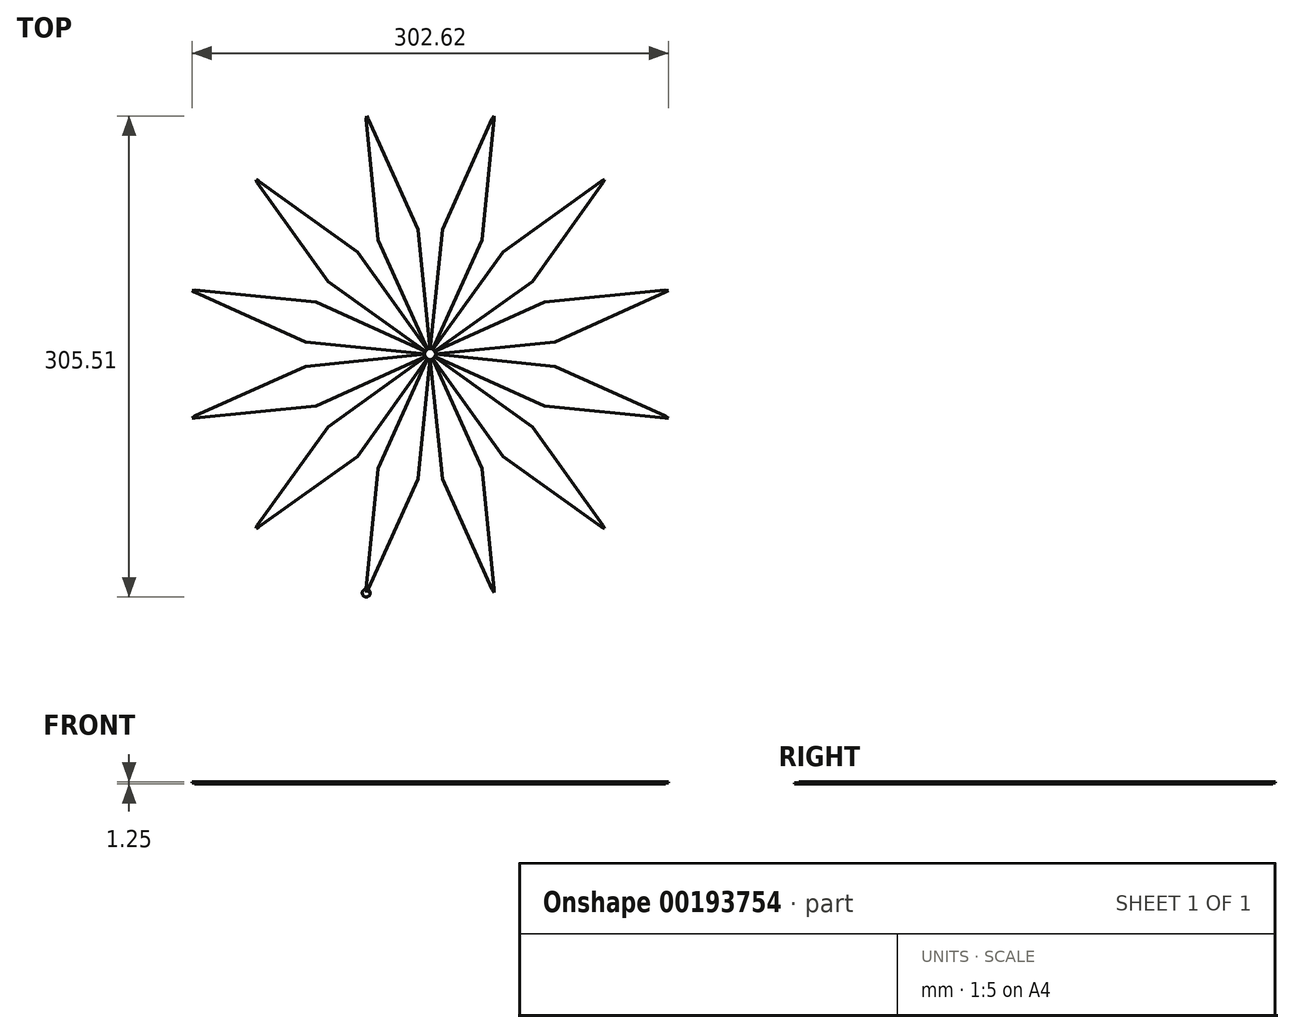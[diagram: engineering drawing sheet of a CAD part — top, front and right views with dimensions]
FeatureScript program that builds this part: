
annotation { "Feature Type Name" : "Feature", "Feature Type Description" : "" }
export const myFeature = defineFeature(function(context is Context, id is Id, definition is map)
    precondition{}
    {
        {
            var Q0;
            Q0=qCreatedBy(makeId("Top.planeOp"),FACE);
            var sketch = newSketch(context, id + "F2", { "sketchPlane" : qUnion([Q0])});
            skCircle(sketch, "E0", {"center": v(0, 0) * mm, "radius": 2.59 * mm});
            skLineSegment(sketch, "E1", {"start": v(0, 0) * mm, "end": v(-1.3, -2.24) * mm});
            skLineSegment(sketch, "E2", {"start": v(0, 0) * mm, "end": v(0, -2.59) * mm});
            skLineSegment(sketch, "E3", {"start": v(2.24, -1.3) * mm, "end": v(2.24, -1.3) * mm});
            skLineSegment(sketch, "E4", {"start": v(1.3, -2.24) * mm, "end": v(1.3, -2.24) * mm});
            skLineSegment(sketch, "E5", {"start": v(0, -2.59) * mm, "end": v(-1.3, -2.24) * mm});
            skLineSegment(sketch, "E6", {"start": v(0, 0) * mm, "end": v(-2.59, 0) * mm});
            skLineSegment(sketch, "E7", {"start": v(0, 0) * mm, "end": v(-2.24, -1.3) * mm});
            skLineSegment(sketch, "E8", {"start": v(-2.59, 0) * mm, "end": v(-2.24, -1.3) * mm});
            skLineSegment(sketch, "E9", {"start": v(-2.24, -1.3) * mm, "end": v(-1.3, -2.24) * mm});
            skLineSegment(sketch, "E10", {"start": v(-1.3, -2.24) * mm, "end": v(-40.67, -149.2) * mm, "construction": true});
            skLineSegment(sketch, "E11", {"start": v(0, -2.59) * mm, "end": v(-39.38, -149.55) * mm, "construction": true});
            skPoint(sketch, "E12", {"position": v(-19.69, -76.07) * mm});
            skPoint(sketch, "E13", {"position": v(-20.98, -75.72) * mm});
            skLineSegment(sketch, "E14", {"start": v(-7.69, -79.28) * mm, "end": v(-32.98, -72.5) * mm, "construction": true});
            skLineSegment(sketch, "E15", {"start": v(-19.69, -76.07) * mm, "end": v(-20.98, -75.72) * mm, "construction": true});
            skPoint(sketch, "E16", {"position": v(-20.34, -75.9) * mm});
            skLineSegment(sketch, "E17", {"start": v(-32.98, -72.5) * mm, "end": v(-40.67, -149.2) * mm});
            skLineSegment(sketch, "E18", {"start": v(-40.67, -149.2) * mm, "end": v(-39.38, -149.55) * mm, "construction": true});
            skLineSegment(sketch, "E19", {"start": v(-39.38, -149.55) * mm, "end": v(-7.69, -79.28) * mm});
            skLineSegment(sketch, "E20", {"start": v(-7.69, -79.28) * mm, "end": v(0, -2.59) * mm});
            skLineSegment(sketch, "E21", {"start": v(-32.98, -72.5) * mm, "end": v(-1.3, -2.24) * mm});
            skLineSegment(sketch, "E22.MirrorCS", {"start": v(-64.82, -46.3) * mm, "end": v(-2.24, -1.3) * mm});
            skLineSegment(sketch, "E23.MirrorCS", {"start": v(-46.3, -64.82) * mm, "end": v(-1.3, -2.24) * mm});
            skLineSegment(sketch, "E24.MirrorCS", {"start": v(-109.82, -108.88) * mm, "end": v(-64.82, -46.3) * mm});
            skLineSegment(sketch, "E25.MirrorCS", {"start": v(-46.3, -64.82) * mm, "end": v(-108.88, -109.82) * mm});
            skLineSegment(sketch, "E26.MirrorCS", {"start": v(-108.88, -109.82) * mm, "end": v(-109.82, -108.88) * mm, "construction": true});
            skLineSegment(sketch, "E27.MirrorCS", {"start": v(-72.5, -32.98) * mm, "end": v(-2.24, -1.3) * mm});
            skLineSegment(sketch, "E28.MirrorCS", {"start": v(-79.28, -7.69) * mm, "end": v(-2.59, 0) * mm});
            skLineSegment(sketch, "E29.MirrorCS", {"start": v(-79.28, -7.69) * mm, "end": v(-149.55, -39.38) * mm});
            skLineSegment(sketch, "E30.MirrorCS", {"start": v(-149.2, -40.67) * mm, "end": v(-72.5, -32.98) * mm});
            skLineSegment(sketch, "E31.MirrorCS", {"start": v(-149.55, -39.38) * mm, "end": v(-149.2, -40.67) * mm, "construction": true});
            skLineSegment(sketch, "E32.MirrorCS", {"start": v(7.69, -79.28) * mm, "end": v(0, -2.59) * mm});
            skLineSegment(sketch, "E33.MirrorCS", {"start": v(39.38, -149.55) * mm, "end": v(7.69, -79.28) * mm});
            skLineSegment(sketch, "E34.MirrorCS", {"start": v(32.98, -72.5) * mm, "end": v(40.67, -149.2) * mm});
            skLineSegment(sketch, "E35.MirrorCS", {"start": v(32.98, -72.5) * mm, "end": v(1.3, -2.24) * mm});
            skLineSegment(sketch, "E36.MirrorCS", {"start": v(40.67, -149.2) * mm, "end": v(39.38, -149.55) * mm, "construction": true});
            skLineSegment(sketch, "E37.MirrorCS", {"start": v(46.3, -64.82) * mm, "end": v(1.3, -2.24) * mm});
            skLineSegment(sketch, "E38.MirrorCS", {"start": v(109.82, -108.88) * mm, "end": v(64.82, -46.3) * mm});
            skLineSegment(sketch, "E39.MirrorCS", {"start": v(46.3, -64.82) * mm, "end": v(108.88, -109.82) * mm});
            skLineSegment(sketch, "E40.MirrorCS", {"start": v(64.82, -46.3) * mm, "end": v(2.24, -1.3) * mm});
            skLineSegment(sketch, "E41.MirrorCS", {"start": v(108.88, -109.82) * mm, "end": v(109.82, -108.88) * mm, "construction": true});
            skLineSegment(sketch, "E42.MirrorCS", {"start": v(72.5, -32.98) * mm, "end": v(2.24, -1.3) * mm});
            skLineSegment(sketch, "E43.MirrorCS", {"start": v(149.2, -40.67) * mm, "end": v(72.5, -32.98) * mm});
            skLineSegment(sketch, "E44.MirrorCS", {"start": v(79.28, -7.69) * mm, "end": v(2.59, 0) * mm});
            skLineSegment(sketch, "E45.MirrorCS", {"start": v(79.28, -7.69) * mm, "end": v(149.55, -39.38) * mm});
            skLineSegment(sketch, "E46.MirrorCS", {"start": v(149.55, -39.38) * mm, "end": v(149.2, -40.67) * mm, "construction": true});
            skLineSegment(sketch, "E47.MirrorCS", {"start": v(-79.28, 7.69) * mm, "end": v(-2.59, 0) * mm});
            skLineSegment(sketch, "E48.MirrorCS", {"start": v(-72.5, 32.98) * mm, "end": v(-2.24, 1.3) * mm});
            skLineSegment(sketch, "E49.MirrorCS", {"start": v(-64.82, 46.3) * mm, "end": v(-2.24, 1.3) * mm});
            skLineSegment(sketch, "E50.MirrorCS", {"start": v(-46.3, 64.82) * mm, "end": v(-1.3, 2.24) * mm});
            skLineSegment(sketch, "E51.MirrorCS", {"start": v(-32.98, 72.5) * mm, "end": v(-1.3, 2.24) * mm});
            skLineSegment(sketch, "E52.MirrorCS", {"start": v(-7.69, 79.28) * mm, "end": v(0, 2.59) * mm});
            skLineSegment(sketch, "E53.MirrorCS", {"start": v(7.69, 79.28) * mm, "end": v(0, 2.59) * mm});
            skLineSegment(sketch, "E54.MirrorCS", {"start": v(32.98, 72.5) * mm, "end": v(1.3, 2.24) * mm});
            skLineSegment(sketch, "E55.MirrorCS", {"start": v(64.82, 46.3) * mm, "end": v(2.24, 1.3) * mm});
            skLineSegment(sketch, "E56.MirrorCS", {"start": v(72.5, 32.98) * mm, "end": v(2.24, 1.3) * mm});
            skLineSegment(sketch, "E57.MirrorCS", {"start": v(79.28, 7.69) * mm, "end": v(2.59, 0) * mm});
            skLineSegment(sketch, "E58.MirrorCS", {"start": v(46.3, 64.82) * mm, "end": v(1.3, 2.24) * mm});
            skLineSegment(sketch, "E59.MirrorCS", {"start": v(-79.28, 7.69) * mm, "end": v(-149.55, 39.38) * mm});
            skLineSegment(sketch, "E60.MirrorCS", {"start": v(-149.2, 40.67) * mm, "end": v(-72.5, 32.98) * mm});
            skLineSegment(sketch, "E61.MirrorCS", {"start": v(-149.55, 39.38) * mm, "end": v(-149.2, 40.67) * mm, "construction": true});
            skLineSegment(sketch, "E62.MirrorCS", {"start": v(-109.82, 108.88) * mm, "end": v(-64.82, 46.3) * mm});
            skLineSegment(sketch, "E63.MirrorCS", {"start": v(-46.3, 64.82) * mm, "end": v(-108.88, 109.82) * mm});
            skLineSegment(sketch, "E64.MirrorCS", {"start": v(-108.88, 109.82) * mm, "end": v(-109.82, 108.88) * mm, "construction": true});
            skLineSegment(sketch, "E65.MirrorCS", {"start": v(-32.98, 72.5) * mm, "end": v(-40.67, 149.2) * mm});
            skLineSegment(sketch, "E66.MirrorCS", {"start": v(-39.38, 149.55) * mm, "end": v(-7.69, 79.28) * mm});
            skLineSegment(sketch, "E67.MirrorCS", {"start": v(39.38, 149.55) * mm, "end": v(7.69, 79.28) * mm});
            skLineSegment(sketch, "E68.MirrorCS", {"start": v(32.98, 72.5) * mm, "end": v(40.67, 149.2) * mm});
            skLineSegment(sketch, "E69.MirrorCS", {"start": v(46.3, 64.82) * mm, "end": v(108.88, 109.82) * mm});
            skLineSegment(sketch, "E70.MirrorCS", {"start": v(109.82, 108.88) * mm, "end": v(64.82, 46.3) * mm});
            skLineSegment(sketch, "E71.MirrorCS", {"start": v(149.2, 40.67) * mm, "end": v(72.5, 32.98) * mm});
            skLineSegment(sketch, "E72.MirrorCS", {"start": v(79.28, 7.69) * mm, "end": v(149.55, 39.38) * mm});
            skLineSegment(sketch, "E73.MirrorCS", {"start": v(149.55, 39.38) * mm, "end": v(149.2, 40.67) * mm, "construction": true});
            skLineSegment(sketch, "E74.MirrorCS", {"start": v(108.88, 109.82) * mm, "end": v(109.82, 108.88) * mm, "construction": true});
            skLineSegment(sketch, "E75.MirrorCS", {"start": v(40.67, 149.2) * mm, "end": v(39.38, 149.55) * mm, "construction": true});
            skLineSegment(sketch, "E76.MirrorCS", {"start": v(-40.67, 149.2) * mm, "end": v(-39.38, 149.55) * mm, "construction": true});
            skLineSegment(sketch, "E77", {"start": v(-39.38, -149.55) * mm, "end": v(-40.54, -151.3) * mm});
            skLineSegment(sketch, "E78", {"start": v(-40.54, -151.3) * mm, "end": v(-40.67, -149.2) * mm});
            skLineSegment(sketch, "E79.MirrorCS", {"start": v(-109.82, -108.88) * mm, "end": v(-110.76, -110.76) * mm});
            skLineSegment(sketch, "E80.MirrorCS", {"start": v(-110.76, -110.76) * mm, "end": v(-108.88, -109.82) * mm});
            skLineSegment(sketch, "E81.MirrorCS", {"start": v(-151.3, -40.54) * mm, "end": v(-149.55, -39.38) * mm});
            skLineSegment(sketch, "E82.MirrorCS", {"start": v(-149.2, -40.67) * mm, "end": v(-151.3, -40.54) * mm});
            skLineSegment(sketch, "E83.MirrorCS", {"start": v(39.38, -149.55) * mm, "end": v(40.54, -151.3) * mm});
            skLineSegment(sketch, "E84.MirrorCS", {"start": v(40.54, -151.3) * mm, "end": v(40.67, -149.2) * mm});
            skLineSegment(sketch, "E85.MirrorCS", {"start": v(109.82, -108.88) * mm, "end": v(110.76, -110.76) * mm});
            skLineSegment(sketch, "E86.MirrorCS", {"start": v(110.76, -110.76) * mm, "end": v(108.88, -109.82) * mm});
            skLineSegment(sketch, "E87.MirrorCS", {"start": v(151.3, -40.54) * mm, "end": v(149.55, -39.38) * mm});
            skLineSegment(sketch, "E88.MirrorCS", {"start": v(149.2, -40.67) * mm, "end": v(151.3, -40.54) * mm});
            skLineSegment(sketch, "E89.MirrorCS", {"start": v(-151.3, 40.54) * mm, "end": v(-149.55, 39.38) * mm});
            skLineSegment(sketch, "E90.MirrorCS", {"start": v(-149.2, 40.67) * mm, "end": v(-151.3, 40.54) * mm});
            skLineSegment(sketch, "E91.MirrorCS", {"start": v(-109.82, 108.88) * mm, "end": v(-110.76, 110.76) * mm});
            skLineSegment(sketch, "E92.MirrorCS", {"start": v(-110.76, 110.76) * mm, "end": v(-108.88, 109.82) * mm});
            skLineSegment(sketch, "E93.MirrorCS", {"start": v(-40.54, 151.3) * mm, "end": v(-40.67, 149.2) * mm});
            skLineSegment(sketch, "E94.MirrorCS", {"start": v(-39.38, 149.55) * mm, "end": v(-40.54, 151.3) * mm});
            skLineSegment(sketch, "E95.MirrorCS", {"start": v(39.38, 149.55) * mm, "end": v(40.54, 151.3) * mm});
            skLineSegment(sketch, "E96.MirrorCS", {"start": v(40.54, 151.3) * mm, "end": v(40.67, 149.2) * mm});
            skLineSegment(sketch, "E97.MirrorCS", {"start": v(109.82, 108.88) * mm, "end": v(110.76, 110.76) * mm});
            skLineSegment(sketch, "E98.MirrorCS", {"start": v(110.76, 110.76) * mm, "end": v(108.88, 109.82) * mm});
            skLineSegment(sketch, "E99.MirrorCS", {"start": v(151.3, 40.54) * mm, "end": v(149.55, 39.38) * mm});
            skLineSegment(sketch, "E100.MirrorCS", {"start": v(149.2, 40.67) * mm, "end": v(151.3, 40.54) * mm});
            skSolve(sketch);
        }
        {
            var Q0;
            Q0 = qSketchRegion(id + "F2", true);
            extrude(context, id + "F0", {"entities" : qUnion([Q0]), "depth" : 1.25 * mm});
        }
        {
            var Q0;
            Q0=makeQuery(id+"F2.imprint","IMPRINT",FACE,{"disambiguationData":[TD([[makeQuery(id+"F2.imprint","IMPRINT",EDGE,{"derivedFrom":sQuery(id+"F2.wireOp",EDGE,"E19")}),1.0]])]});
            var sketch = newSketch(context, id + "F3", { "sketchPlane" : qUnion([Q0])});
            skCircle(sketch, "E101", {"center": v(-40.65, -151.7) * mm, "radius": 2.5 * mm});
            skSolve(sketch);
        }
        {
            var Q0;
            {var subQ1=makeQuery(id+"F2.imprint","IMPRINT",EDGE,{"derivedFrom":sQuery(id+"F2.wireOp",EDGE,"E77")});Q0=makeQuery(id+"F3.imprint","IMPRINT",FACE,{"disambiguationData":[TD([[makeQuery(id+"F3.imprint","IMPRINT",EDGE,{"derivedFrom":subQ1}),1.0]])]});}
            var Q1;
            {var subQ1=makeQuery(id+"F2.imprint","IMPRINT",EDGE,{"derivedFrom":sQuery(id+"F2.wireOp",EDGE,"E77")});Q1=makeQuery(id+"F3.imprint","IMPRINT",FACE,{"disambiguationData":[TD([[makeQuery(id+"F3.imprint","IMPRINT",EDGE,{"derivedFrom":subQ1}),-1.0]])]});}
            var Q2;
            Q2=sQuery(id+"F3.wireOp",EDGE,"E101");
            extrude(context, id + "F4", {"entities" : qUnion([Q0, Q1]), "operationType" : NewBodyOperationType.ADD, "surfaceEntities" : qUnion([Q2]), "depth" : 0.5 * mm});
        }
        {
            var Q0;
            Q0=makeQuery(id+"F4.boolean.opBoolean","MERGE",FACE,{"derivedFrom":[makeQuery(id+"F0.opExtrude","CAP_FACE",FACE,{"disambiguationData":[OSD([sQuery(id+"F2.wireOp",EDGE,"E19"),sQuery(id+"F2.wireOp",EDGE,"E20"),sQuery(id+"F2.wireOp",EDGE,"E21"),sQuery(id+"F2.wireOp",EDGE,"E22.MirrorCS"),sQuery(id+"F2.wireOp",EDGE,"E23.MirrorCS"),sQuery(id+"F2.wireOp",EDGE,"E24.MirrorCS"),sQuery(id+"F2.wireOp",EDGE,"E25.MirrorCS"),sQuery(id+"F2.wireOp",EDGE,"E27.MirrorCS"),sQuery(id+"F2.wireOp",EDGE,"E28.MirrorCS"),sQuery(id+"F2.wireOp",EDGE,"E29.MirrorCS"),sQuery(id+"F2.wireOp",EDGE,"E30.MirrorCS"),sQuery(id+"F2.wireOp",EDGE,"E32.MirrorCS"),sQuery(id+"F2.wireOp",EDGE,"E33.MirrorCS"),sQuery(id+"F2.wireOp",EDGE,"E17"),sQuery(id+"F2.wireOp",EDGE,"E34.MirrorCS"),sQuery(id+"F2.wireOp",EDGE,"E35.MirrorCS"),sQuery(id+"F2.wireOp",EDGE,"E37.MirrorCS"),sQuery(id+"F2.wireOp",EDGE,"E38.MirrorCS"),sQuery(id+"F2.wireOp",EDGE,"E39.MirrorCS"),sQuery(id+"F2.wireOp",EDGE,"E40.MirrorCS"),sQuery(id+"F2.wireOp",EDGE,"E42.MirrorCS"),sQuery(id+"F2.wireOp",EDGE,"E43.MirrorCS"),sQuery(id+"F2.wireOp",EDGE,"E44.MirrorCS"),sQuery(id+"F2.wireOp",EDGE,"E45.MirrorCS"),sQuery(id+"F2.wireOp",EDGE,"E47.MirrorCS"),sQuery(id+"F2.wireOp",EDGE,"E48.MirrorCS"),sQuery(id+"F2.wireOp",EDGE,"E49.MirrorCS"),sQuery(id+"F2.wireOp",EDGE,"E50.MirrorCS"),sQuery(id+"F2.wireOp",EDGE,"E51.MirrorCS"),sQuery(id+"F2.wireOp",EDGE,"E52.MirrorCS"),sQuery(id+"F2.wireOp",EDGE,"E53.MirrorCS"),sQuery(id+"F2.wireOp",EDGE,"E54.MirrorCS"),sQuery(id+"F2.wireOp",EDGE,"E55.MirrorCS"),sQuery(id+"F2.wireOp",EDGE,"E56.MirrorCS"),sQuery(id+"F2.wireOp",EDGE,"E57.MirrorCS"),sQuery(id+"F2.wireOp",EDGE,"E58.MirrorCS"),sQuery(id+"F2.wireOp",EDGE,"E59.MirrorCS"),sQuery(id+"F2.wireOp",EDGE,"E60.MirrorCS"),sQuery(id+"F2.wireOp",EDGE,"E62.MirrorCS"),sQuery(id+"F2.wireOp",EDGE,"E63.MirrorCS"),sQuery(id+"F2.wireOp",EDGE,"E65.MirrorCS"),sQuery(id+"F2.wireOp",EDGE,"E66.MirrorCS"),sQuery(id+"F2.wireOp",EDGE,"E67.MirrorCS"),sQuery(id+"F2.wireOp",EDGE,"E68.MirrorCS"),sQuery(id+"F2.wireOp",EDGE,"E69.MirrorCS"),sQuery(id+"F2.wireOp",EDGE,"E70.MirrorCS"),sQuery(id+"F2.wireOp",EDGE,"E71.MirrorCS"),sQuery(id+"F2.wireOp",EDGE,"E72.MirrorCS"),sQuery(id+"F2.wireOp",EDGE,"E77"),sQuery(id+"F2.wireOp",EDGE,"E78"),sQuery(id+"F2.wireOp",EDGE,"E79.MirrorCS"),sQuery(id+"F2.wireOp",EDGE,"E80.MirrorCS"),sQuery(id+"F2.wireOp",EDGE,"E82.MirrorCS"),sQuery(id+"F2.wireOp",EDGE,"E81.MirrorCS"),sQuery(id+"F2.wireOp",EDGE,"E84.MirrorCS"),sQuery(id+"F2.wireOp",EDGE,"E83.MirrorCS"),sQuery(id+"F2.wireOp",EDGE,"E86.MirrorCS"),sQuery(id+"F2.wireOp",EDGE,"E85.MirrorCS"),sQuery(id+"F2.wireOp",EDGE,"E87.MirrorCS"),sQuery(id+"F2.wireOp",EDGE,"E88.MirrorCS"),sQuery(id+"F2.wireOp",EDGE,"E89.MirrorCS"),sQuery(id+"F2.wireOp",EDGE,"E90.MirrorCS"),sQuery(id+"F2.wireOp",EDGE,"E91.MirrorCS"),sQuery(id+"F2.wireOp",EDGE,"E92.MirrorCS"),sQuery(id+"F2.wireOp",EDGE,"E93.MirrorCS"),sQuery(id+"F2.wireOp",EDGE,"E94.MirrorCS"),sQuery(id+"F2.wireOp",EDGE,"E95.MirrorCS"),sQuery(id+"F2.wireOp",EDGE,"E96.MirrorCS"),sQuery(id+"F2.wireOp",EDGE,"E97.MirrorCS"),sQuery(id+"F2.wireOp",EDGE,"E98.MirrorCS"),sQuery(id+"F2.wireOp",EDGE,"E99.MirrorCS"),sQuery(id+"F2.wireOp",EDGE,"E100.MirrorCS")])],"isStart":true}),makeQuery(id+"F4.opExtrude","CAP_FACE",FACE,{"disambiguationData":[OSD([sQuery(id+"F3.wireOp",EDGE,"E101")])],"isStart":true})]});
            var sketch = newSketch(context, id + "F5", { "sketchPlane" : qUnion([Q0])});
            skLineSegment(sketch, "E102", {"start": v(40.54, 151.3) * mm, "end": v(40.67, 149.2) * mm});
            skLineSegment(sketch, "E103", {"start": v(39.38, 149.55) * mm, "end": v(40.67, 149.2) * mm});
            skLineSegment(sketch, "E104", {"start": v(40.54, 151.3) * mm, "end": v(39.38, 149.55) * mm});
            skLineSegment(sketch, "E105", {"start": v(110.76, 110.76) * mm, "end": v(109.82, 108.88) * mm});
            skLineSegment(sketch, "E106", {"start": v(108.88, 109.82) * mm, "end": v(109.82, 108.88) * mm});
            skLineSegment(sketch, "E107", {"start": v(108.88, 109.82) * mm, "end": v(110.76, 110.76) * mm});
            skLineSegment(sketch, "E108", {"start": v(149.2, 40.67) * mm, "end": v(149.55, 39.38) * mm});
            skLineSegment(sketch, "E109", {"start": v(151.3, 40.54) * mm, "end": v(149.55, 39.38) * mm});
            skLineSegment(sketch, "E110", {"start": v(149.2, 40.67) * mm, "end": v(151.3, 40.54) * mm});
            skLineSegment(sketch, "E111", {"start": v(149.2, -40.67) * mm, "end": v(149.55, -39.38) * mm});
            skLineSegment(sketch, "E112", {"start": v(149.55, -39.38) * mm, "end": v(149.55, -39.38) * mm});
            skLineSegment(sketch, "E113", {"start": v(149.2, -40.67) * mm, "end": v(151.3, -40.54) * mm});
            skLineSegment(sketch, "E114", {"start": v(151.3, -40.54) * mm, "end": v(149.55, -39.38) * mm});
            skLineSegment(sketch, "E115", {"start": v(108.88, -109.82) * mm, "end": v(110.76, -110.76) * mm});
            skLineSegment(sketch, "E116", {"start": v(110.76, -110.76) * mm, "end": v(109.82, -108.88) * mm});
            skLineSegment(sketch, "E117", {"start": v(109.82, -108.88) * mm, "end": v(108.88, -109.82) * mm});
            skLineSegment(sketch, "E118", {"start": v(40.67, -149.2) * mm, "end": v(39.38, -149.55) * mm});
            skLineSegment(sketch, "E119", {"start": v(39.38, -149.55) * mm, "end": v(40.54, -151.3) * mm});
            skLineSegment(sketch, "E120", {"start": v(40.54, -151.3) * mm, "end": v(40.54, -151.3) * mm});
            skLineSegment(sketch, "E121", {"start": v(40.67, -149.2) * mm, "end": v(40.54, -151.3) * mm});
            skLineSegment(sketch, "E122", {"start": v(-39.38, -149.55) * mm, "end": v(-40.54, -151.3) * mm});
            skLineSegment(sketch, "E123", {"start": v(-40.54, -151.3) * mm, "end": v(-40.67, -149.2) * mm});
            skLineSegment(sketch, "E124", {"start": v(-40.67, -149.2) * mm, "end": v(-39.38, -149.55) * mm});
            skLineSegment(sketch, "E125", {"start": v(-110.76, -110.76) * mm, "end": v(-108.88, -109.82) * mm});
            skLineSegment(sketch, "E126", {"start": v(-108.88, -109.82) * mm, "end": v(-108.88, -109.82) * mm});
            skLineSegment(sketch, "E127", {"start": v(-108.88, -109.82) * mm, "end": v(-110.76, -110.76) * mm});
            skLineSegment(sketch, "E128", {"start": v(-109.82, -108.88) * mm, "end": v(-108.88, -109.82) * mm});
            skLineSegment(sketch, "E129", {"start": v(-109.82, -108.88) * mm, "end": v(-110.76, -110.76) * mm});
            skLineSegment(sketch, "E130", {"start": v(-149.55, -39.38) * mm, "end": v(-151.3, -40.54) * mm});
            skLineSegment(sketch, "E131", {"start": v(-151.3, -40.54) * mm, "end": v(-149.2, -40.67) * mm});
            skLineSegment(sketch, "E132", {"start": v(-149.2, -40.67) * mm, "end": v(-149.2, -40.67) * mm});
            skLineSegment(sketch, "E133", {"start": v(-149.55, -39.38) * mm, "end": v(-149.2, -40.67) * mm});
            skLineSegment(sketch, "E134", {"start": v(-149.2, 40.67) * mm, "end": v(-149.55, 39.38) * mm});
            skLineSegment(sketch, "E135", {"start": v(-149.55, 39.38) * mm, "end": v(-149.55, 39.38) * mm});
            skLineSegment(sketch, "E136", {"start": v(-149.55, 39.38) * mm, "end": v(-151.3, 40.54) * mm});
            skLineSegment(sketch, "E137", {"start": v(-151.3, 40.54) * mm, "end": v(-151.3, 40.54) * mm});
            skLineSegment(sketch, "E138", {"start": v(-151.3, 40.54) * mm, "end": v(-149.2, 40.67) * mm});
            skLineSegment(sketch, "E139", {"start": v(-108.88, 109.82) * mm, "end": v(-110.76, 110.76) * mm});
            skLineSegment(sketch, "E140", {"start": v(-110.76, 110.76) * mm, "end": v(-109.82, 108.88) * mm});
            skLineSegment(sketch, "E141", {"start": v(-109.82, 108.88) * mm, "end": v(-108.88, 109.82) * mm});
            skSolve(sketch);
        }
        {
            var Q0;
            Q0 = qSketchRegion(id + "F5", true);
            extrude(context, id + "F1", {"entities" : qUnion([Q0]), "operationType" : NewBodyOperationType.REMOVE, "oppositeDirection" : true, "depth" : 0.62 * mm});
        }
    });
